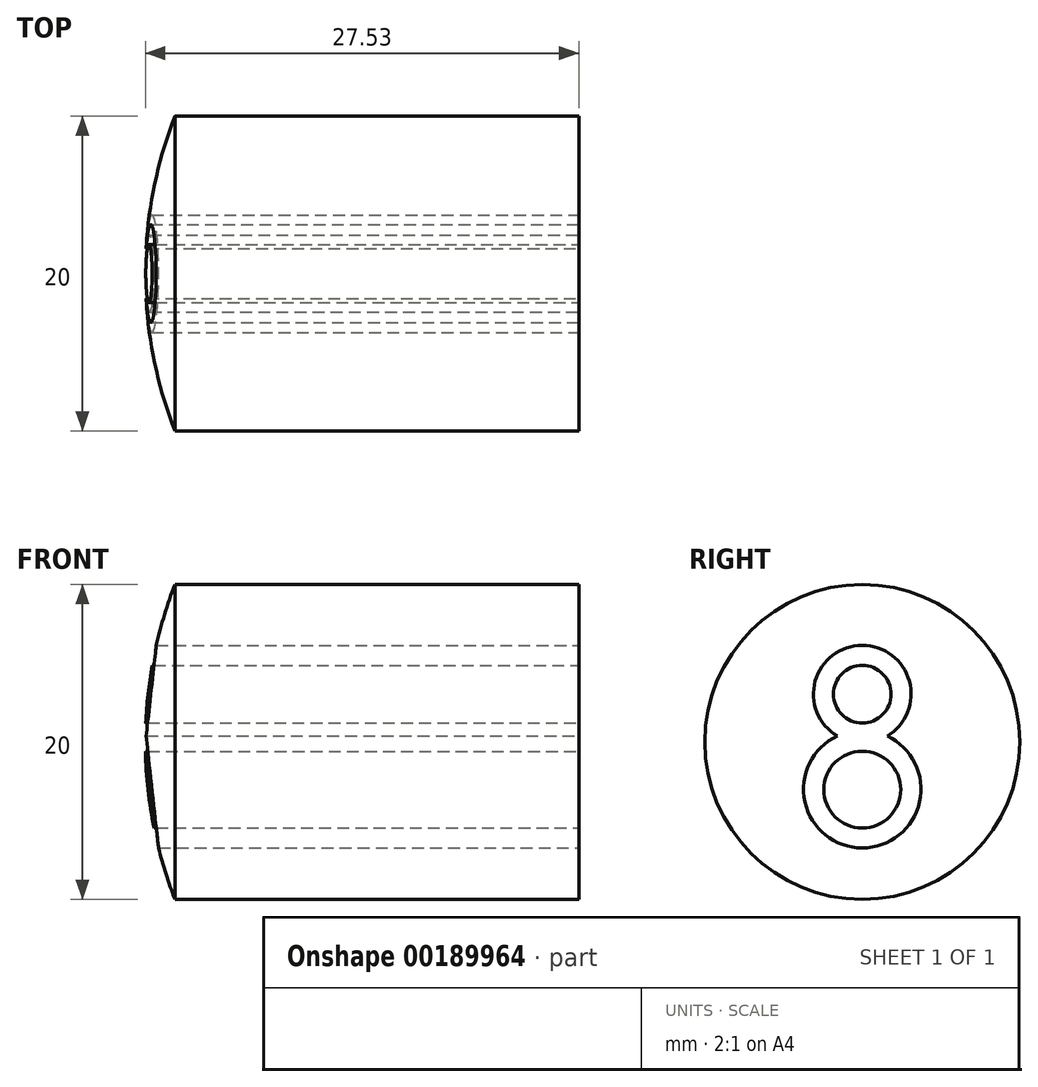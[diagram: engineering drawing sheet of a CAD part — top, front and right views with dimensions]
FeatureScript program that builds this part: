
annotation { "Feature Type Name" : "Feature", "Feature Type Description" : "" }
export const myFeature = defineFeature(function(context is Context, id is Id, definition is map)
    precondition{}
    {
        {
            var Q0;
            Q0=qCreatedBy(makeId("Front.planeOp"),FACE);
            var sketch = newSketch(context, id + "F0", { "sketchPlane" : qUnion([Q0])});
            skLineSegment(sketch, "E0.bottom", {"start": v(0, 0) * mm, "end": v(-27.53, 0) * mm});
            skLineSegment(sketch, "E0.top", {"start": v(0, 10) * mm, "end": v(-25.65, 10) * mm});
            skLineSegment(sketch, "E0.left", {"start": v(0, 0) * mm, "end": v(0, 10) * mm});
            skArc(sketch, "E1", {"start": v(-25.65, 10) * mm, "mid": v(-27.06, 5.09) * mm, "end": v(-27.53, 0) * mm});
            skSolve(sketch);
        }
        {
            var Q0;
            Q0 = qSketchRegion(id + "F0", true);
            var Q1;
            Q1=sQuery(id+"F0.wireOp",EDGE,"E0.bottom");
            revolve(context, id + "F1", {"entities" : qUnion([Q0]), "axis" : qUnion([Q1]), "revolveType" : RevolveType.FULL});
        }
        {
            var Q0;
            Q0=makeQuery(id+"F1.opRevolve","SWEPT_FACE",FACE,{"disambiguationData":[OSD([sQuery(id+"F0.wireOp",EDGE,"E0.left")])]});
            var sketch = newSketch(context, id + "F2", { "sketchPlane" : qUnion([Q0])});
            skCircle(sketch, "E2", {"center": v(0, -0.06) * mm, "radius": 10 * mm});
            skArc(sketch, "E3", {"start": v(1.58, 0.37) * mm, "mid": v(0, 6.14) * mm, "end": v(-1.58, 0.37) * mm});
            skArc(sketch, "E4", {"start": v(-1.58, 0.37) * mm, "mid": v(0, -6.74) * mm, "end": v(1.58, 0.37) * mm});
            skCircle(sketch, "E5", {"center": v(0, 3.03) * mm, "radius": 1.83 * mm});
            skCircle(sketch, "E6", {"center": v(0, -3.03) * mm, "radius": 2.44 * mm});
            skSolve(sketch);
        }
        {
            var Q0;
            Q0=makeQuery(id+"F2.imprint","IMPRINT",FACE,{"disambiguationData":[TD([[makeQuery(id+"F2.imprint","IMPRINT",EDGE,{"derivedFrom":sQuery(id+"F2.wireOp",EDGE,"E3")}),1.0]])]});
            extrude(context, id + "F3", {"entities" : qUnion([Q0]), "operationType" : NewBodyOperationType.REMOVE, "endBound" : BoundingType.UP_TO_NEXT, "oppositeDirection" : true, "depth" : 25 * mm});
        }
    });
